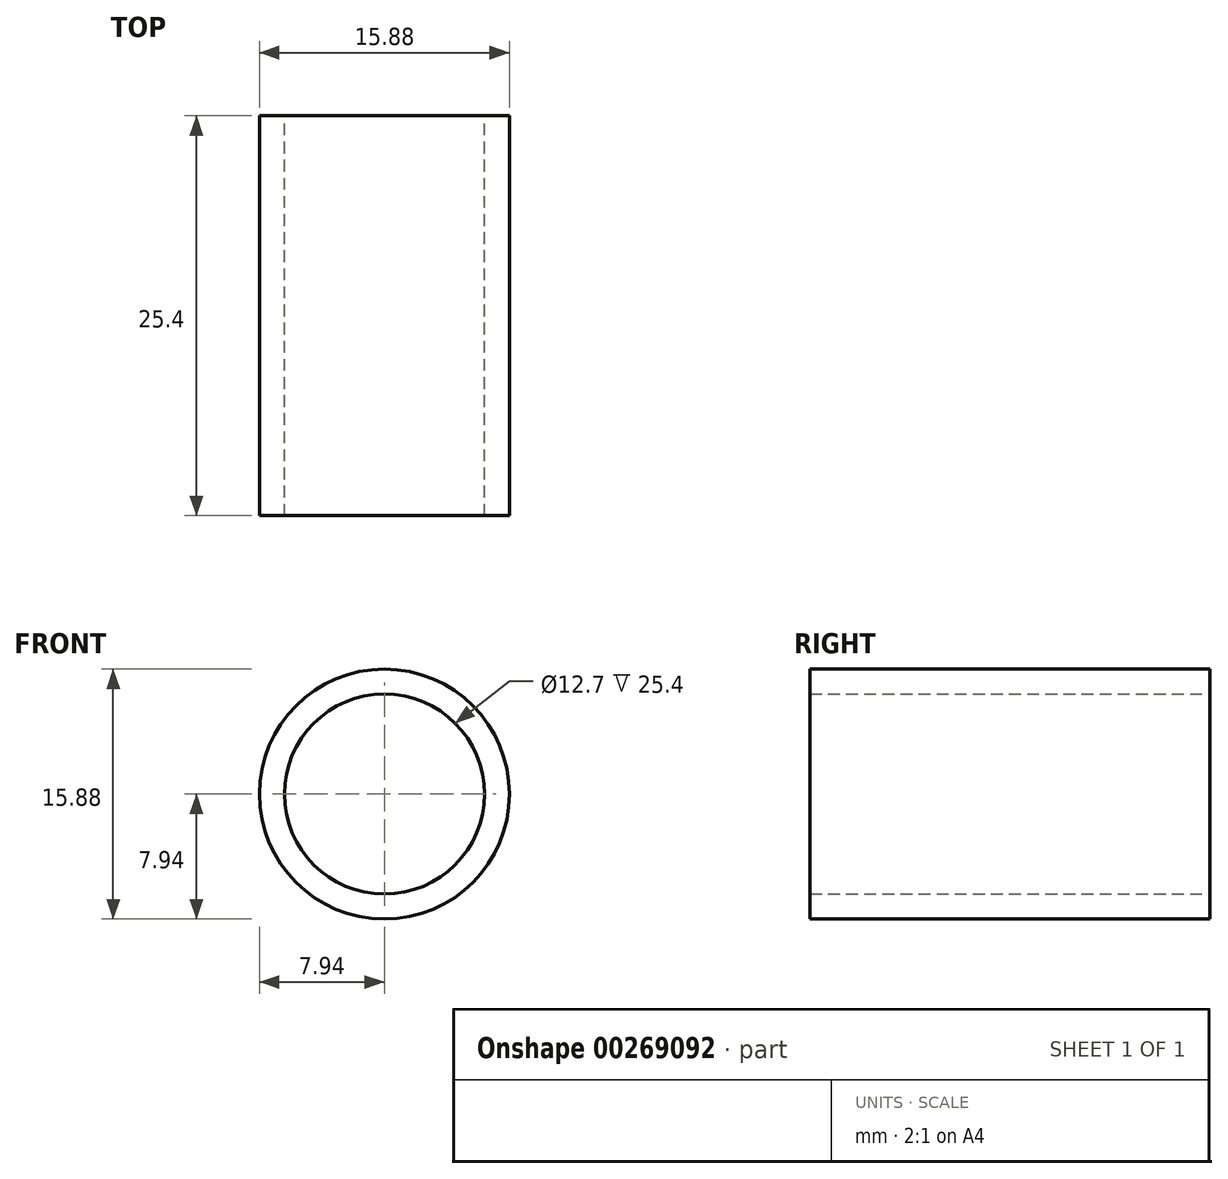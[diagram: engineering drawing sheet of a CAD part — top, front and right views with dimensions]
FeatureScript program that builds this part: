
annotation { "Feature Type Name" : "Feature", "Feature Type Description" : "" }
export const myFeature = defineFeature(function(context is Context, id is Id, definition is map)
    precondition{}
    {
        {
            var Q0;
            Q0=qCreatedBy(makeId("Front.planeOp"),FACE);
            var sketch = newSketch(context, id + "F0", { "sketchPlane" : qUnion([Q0])});
            skCircle(sketch, "E0", {"center": v(0, 0) * mm, "radius": 6.35 * mm});
            skCircle(sketch, "E1", {"center": v(0, 0) * mm, "radius": 7.94 * mm});
            skSolve(sketch);
        }
        {
            var Q0;
            Q0 = qSketchRegion(id + "F0", true);
            extrude(context, id + "F1", {"entities" : qUnion([Q0]), "depth" : 25.4 * mm});
        }
    });
